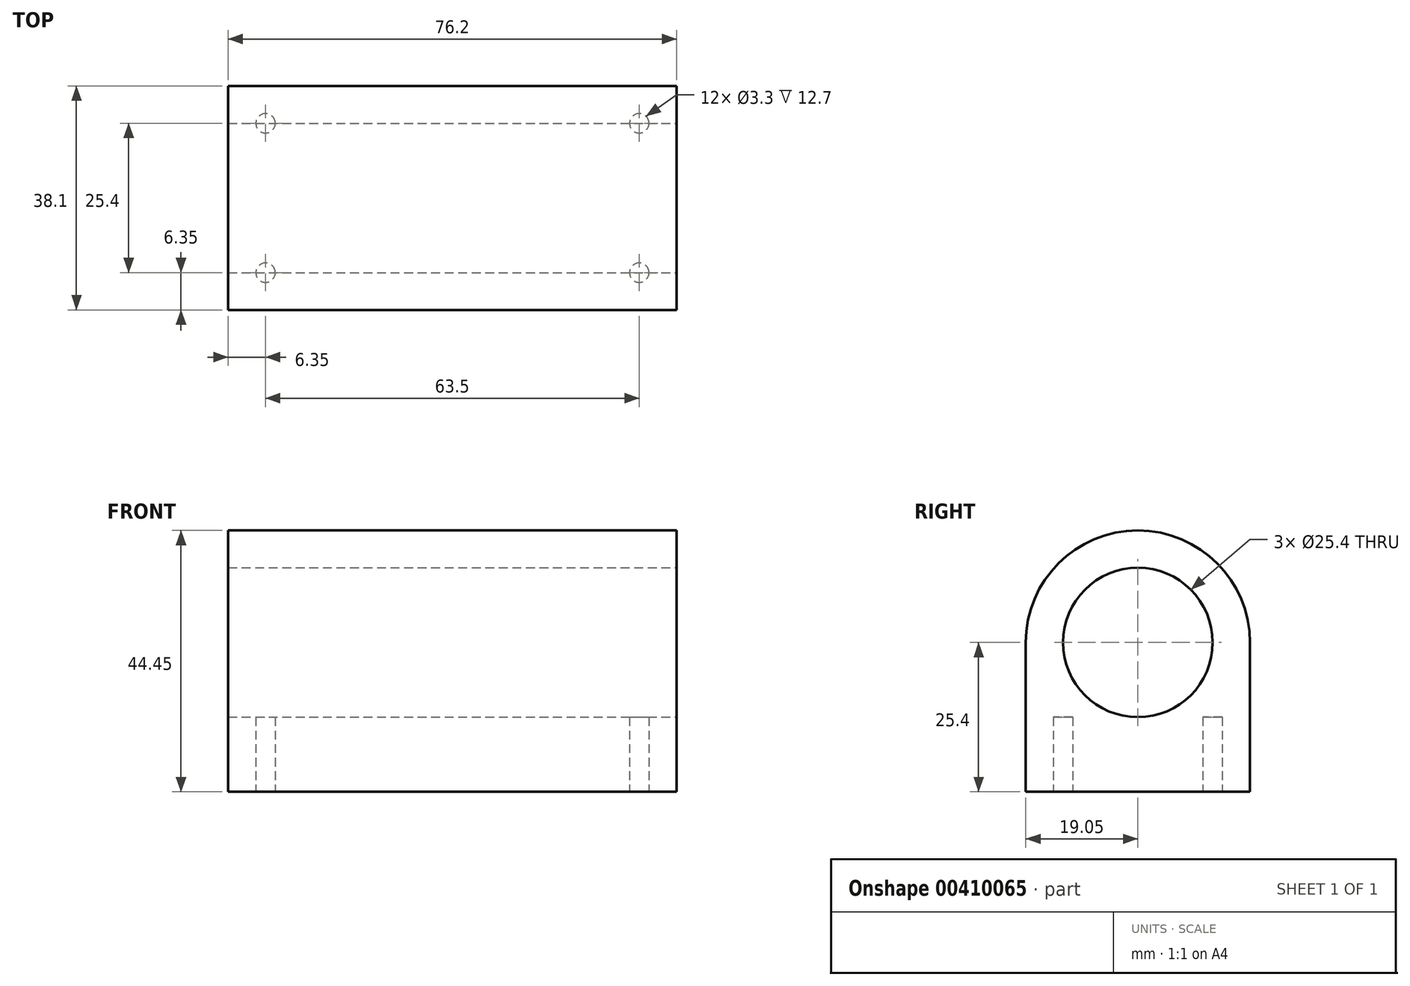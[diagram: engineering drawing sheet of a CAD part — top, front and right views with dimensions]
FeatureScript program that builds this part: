
annotation { "Feature Type Name" : "Feature", "Feature Type Description" : "" }
export const myFeature = defineFeature(function(context is Context, id is Id, definition is map)
    precondition{}
    {
        {
            var Q0;
            Q0=qCreatedBy(makeId("Right.planeOp"),FACE);
            var sketch = newSketch(context, id + "F0", { "sketchPlane" : qUnion([Q0])});
            skCircle(sketch, "E0", {"center": v(0, 0) * mm, "radius": 12.7 * mm});
            skArc(sketch, "E1", {"start": v(19.05, 0) * mm, "mid": v(0, 19.05) * mm, "end": v(-19.05, 0) * mm});
            skLineSegment(sketch, "E2", {"start": v(-19.05, -25.4) * mm, "end": v(19.05, -25.4) * mm});
            skLineSegment(sketch, "E3", {"start": v(-19.05, 0) * mm, "end": v(-19.05, -25.4) * mm});
            skLineSegment(sketch, "E4", {"start": v(19.05, 0) * mm, "end": v(19.05, -25.4) * mm});
            skSolve(sketch);
        }
        {
            var Q0;
            Q0=makeQuery(id+"F0.imprint","IMPRINT",FACE,{"disambiguationData":[TD([[makeQuery(id+"F0.imprint","IMPRINT",EDGE,{"derivedFrom":sQuery(id+"F0.wireOp",EDGE,"E0")}),-1.0]])]});
            extrude(context, id + "F1", {"entities" : qUnion([Q0]), "oppositeDirection" : true, "depth" : 76.2 * mm});
        }
        {
            var Q0;
            Q0=makeQuery(id+"F1.opExtrude","SWEPT_FACE",FACE,{"disambiguationData":[OSD([sQuery(id+"F0.wireOp",EDGE,"E2")])]});
            var sketch = newSketch(context, id + "F2", { "sketchPlane" : qUnion([Q0])});
            skLineSegment(sketch, "E5.0.0", {"start": v(0, -19.05) * mm, "end": v(0, 19.05) * mm});
            skLineSegment(sketch, "E5.0.1", {"start": v(0, 19.05) * mm, "end": v(-76.2, 19.05) * mm});
            skLineSegment(sketch, "E5.0.2", {"start": v(-76.2, 19.05) * mm, "end": v(-76.2, -19.05) * mm});
            skLineSegment(sketch, "E5.0.3", {"start": v(-76.2, -19.05) * mm, "end": v(0, -19.05) * mm});
            skCircle(sketch, "E6", {"center": v(-69.85, 12.7) * mm, "radius": 1.65 * mm});
            skCircle(sketch, "E7", {"center": v(-69.85, -12.7) * mm, "radius": 1.65 * mm});
            skCircle(sketch, "E8", {"center": v(-6.35, 12.7) * mm, "radius": 1.65 * mm});
            skCircle(sketch, "E9", {"center": v(-6.35, -12.7) * mm, "radius": 1.65 * mm});
            skSolve(sketch);
        }
        {
            var Q0;
            Q0=makeQuery(id+"F2.imprint","IMPRINT",FACE,{"disambiguationData":[TD([[makeQuery(id+"F2.imprint","IMPRINT",EDGE,{"derivedFrom":sQuery(id+"F2.wireOp",EDGE,"E8")}),1.0]])]});
            var Q1;
            Q1=makeQuery(id+"F2.imprint","IMPRINT",FACE,{"disambiguationData":[TD([[makeQuery(id+"F2.imprint","IMPRINT",EDGE,{"derivedFrom":sQuery(id+"F2.wireOp",EDGE,"E9")}),1.0]])]});
            var Q2;
            Q2=makeQuery(id+"F2.imprint","IMPRINT",FACE,{"disambiguationData":[TD([[makeQuery(id+"F2.imprint","IMPRINT",EDGE,{"derivedFrom":sQuery(id+"F2.wireOp",EDGE,"E7")}),1.0]])]});
            var Q3;
            Q3=makeQuery(id+"F2.imprint","IMPRINT",FACE,{"disambiguationData":[TD([[makeQuery(id+"F2.imprint","IMPRINT",EDGE,{"derivedFrom":sQuery(id+"F2.wireOp",EDGE,"E6")}),1.0]])]});
            extrude(context, id + "F3", {"entities" : qUnion([Q0, Q1, Q2, Q3]), "operationType" : NewBodyOperationType.REMOVE, "oppositeDirection" : true, "depth" : 12.7 * mm});
        }
    });
